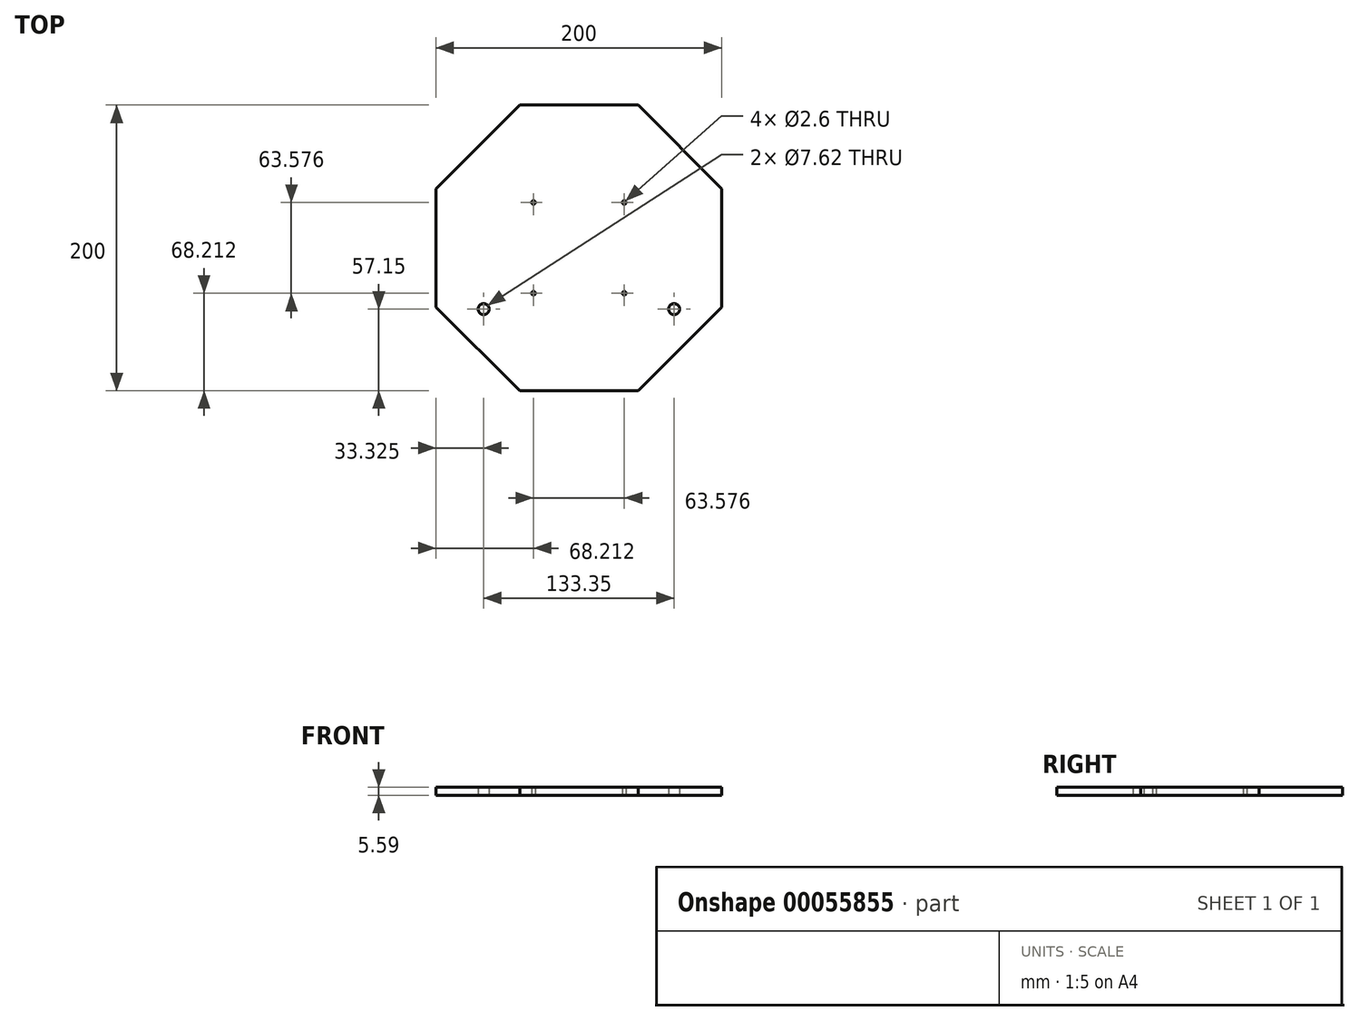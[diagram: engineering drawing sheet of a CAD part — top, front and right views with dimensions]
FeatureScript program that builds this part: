
annotation { "Feature Type Name" : "Feature", "Feature Type Description" : "" }
export const myFeature = defineFeature(function(context is Context, id is Id, definition is map)
    precondition{}
    {
        {
            var Q0;
            Q0=qCreatedBy(makeId("Top.planeOp"),FACE);
            var sketch = newSketch(context, id + "F0", { "sketchPlane" : qUnion([Q0])});
            skCircle(sketch, "E0.cCircle", {"center": v(0, 0) * mm, "radius": 100 * mm, "construction": true});
            skLineSegment(sketch, "E0.0", {"start": v(-41.42, 100) * mm, "end": v(41.42, 100) * mm});
            skLineSegment(sketch, "E0.1", {"start": v(41.42, 100) * mm, "end": v(100, 41.42) * mm});
            skLineSegment(sketch, "E0.2", {"start": v(100, 41.42) * mm, "end": v(100, -41.42) * mm});
            skLineSegment(sketch, "E0.3", {"start": v(100, -41.42) * mm, "end": v(41.42, -100) * mm});
            skLineSegment(sketch, "E0.4", {"start": v(41.42, -100) * mm, "end": v(-41.42, -100) * mm});
            skLineSegment(sketch, "E0.5", {"start": v(-41.42, -100) * mm, "end": v(-100, -41.42) * mm});
            skLineSegment(sketch, "E0.6", {"start": v(-100, -41.42) * mm, "end": v(-100, 41.42) * mm});
            skLineSegment(sketch, "E0.7", {"start": v(-100, 41.42) * mm, "end": v(-41.42, 100) * mm});
            skPoint(sketch, "E0.0.midPoint", {"position": v(0, 100) * mm});
            skCircle(sketch, "E1", {"center": v(-31.79, 31.79) * mm, "radius": 1.3 * mm});
            skCircle(sketch, "E2", {"center": v(31.79, 31.79) * mm, "radius": 1.3 * mm});
            skCircle(sketch, "E3", {"center": v(-31.79, -31.79) * mm, "radius": 1.3 * mm});
            skCircle(sketch, "E4", {"center": v(31.79, -31.79) * mm, "radius": 1.3 * mm});
            skLineSegment(sketch, "E5", {"start": v(0, 0) * mm, "end": v(64.26, 0) * mm});
            skPoint(sketch, "E6", {"position": v(0, -42.85) * mm});
            skLineSegment(sketch, "E7", {"start": v(0, -42.85) * mm, "end": v(66.68, -42.85) * mm});
            skLineSegment(sketch, "E8", {"start": v(0, -42.85) * mm, "end": v(-66.68, -42.85) * mm});
            skCircle(sketch, "E9", {"center": v(-66.68, -42.85) * mm, "radius": 3.81 * mm});
            skCircle(sketch, "E10", {"center": v(66.68, -42.85) * mm, "radius": 3.81 * mm});
            skSolve(sketch);
        }
        {
            var Q0;
            Q0 = qSketchRegion(id + "F0", true);
            extrude(context, id + "F1", {"entities" : qUnion([Q0]), "depth" : 5.6 * mm});
        }
    });
